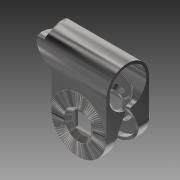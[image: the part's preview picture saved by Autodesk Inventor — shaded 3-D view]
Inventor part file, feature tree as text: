
AUTODESK INVENTOR PART (.ipt)
format: ipt  version: 2013 (Build 170138000, 138)  size: 1,632,256 bytes
history: native  units: mm
features: sketch x13, extrude x12, other x7, fillet x3, revolve x1, pattern_circular x1, mirror x1
ambient origin geometry x8: Origin, YZ Plane, XZ Plane, XY Plane, X Axis, Y Axis, Z Axis, Center Point
feature tree (38):
  other  "Sólido1"
  revolve  "Revolución1"  [1 undecoded]
  extrude  "Extrusión1"  Depth=7.5mm
  extrude  "Extrusión2"  Depth=1.5mm
  other  "Suprimir cara1"
  sketch  "Boceto4"  dims[d8=9.5mm d9=5.0mm]
  sketch  "Boceto5"  dims[d13=5.0mm d15=1.5mm]
  extrude  "Extrusión3"  Depth=5.0mm
  other  "Suprimir cara2"
  other  "Suprimir cara3"
  other  "Suprimir cara4"
  extrude  "Extrusión4"  Depth=1.5mm
  other  "Suprimir cara5"
  extrude  "Extrusión5"  TaperAngle=90.0deg  [1 undecoded]
  other  "Suprimir cara6"
  sketch  "Boceto8"  dims[d22=10.0mm d23=0.0mm d31=21.0mm d32=25.0mm]
  extrude  "Extrusión7"  Depth=9.0mm
  extrude  "Extrusión8"  Depth=21.0mm
  fillet  "Empalme4"  Radius=25.0mm
  extrude  "Extrusión9"  Depth=16.0mm TaperAngle=0.0deg
  pattern_circular  "Patrón circular2"  Count=4  [1 undecoded]
  mirror  "Simetría1"
  extrude  "Extrusión10"  Depth=20.5mm
  extrude  "Extrusión11"  Depth=2.0mm
  extrude  "Extrusión12"  Depth=2.5mm TaperAngle=0.0deg
  extrude  "Extrusión13"  Depth=20.5mm
  fillet  "Empalme5"  Radius=2.5mm
  fillet  "Empalme6"  Radius=0.5mm
  sketch  "Boceto1"  dims[d0=11.0mm d1=1.5mm]
  sketch  "Boceto2"  dims[d4=8.5mm d5=7.5mm]
  sketch  "Boceto3"  dims[d6=11.0mm d7=1.5mm]
  sketch  "Boceto6"  dims[d16=1.5mm d17=90.0deg]
  sketch  "Boceto7"  dims[d20=9.0mm d21=9.0mm]
  sketch  "Boceto9"  dims[d33=22.0mm d34=16.0mm d35=16.0mm d36=0.0mm d37=0.0mm]
  sketch  "Boceto10"  dims[d38=1.5mm d39=40.0mm]
  sketch  "Boceto11"  dims[d40=12.5mm d41=20.5mm]
  sketch  "Boceto12"  dims[d42=20.5mm d43=2.0mm]
  sketch  "Boceto13"  dims[d44=32.0mm d45=0.0mm d46=2.5mm d47=0.0mm d48=20.5mm d49=2.5mm d50=0.0mm d51=0.5mm d52=0.25mm d53=0.25mm d59=2.5mm d60=2.5mm d61=0.0mm d62=0.5mm d63=0.0mm d65=0.5mm d66=0.5mm d67=0.0mm d68=470.0mm d69=360.0deg d71=8.0mm d72=0.0mm d73=1.5mm d74=4.0mm d75=0.0mm d76=1.5mm d77=7.0mm d78=3.5mm d79=0.0mm d80=0.0mm d81=1.5mm d82=7.0mm d83=3.5mm d84=0.0mm d85=0.0mm d86=2.0mm d87=2.0mm]
note: 3 required parameter values undecoded (feature->parameter linkage not recoverable at this tier; creation-order binding heuristic only, values carry confidence <= 0.55)